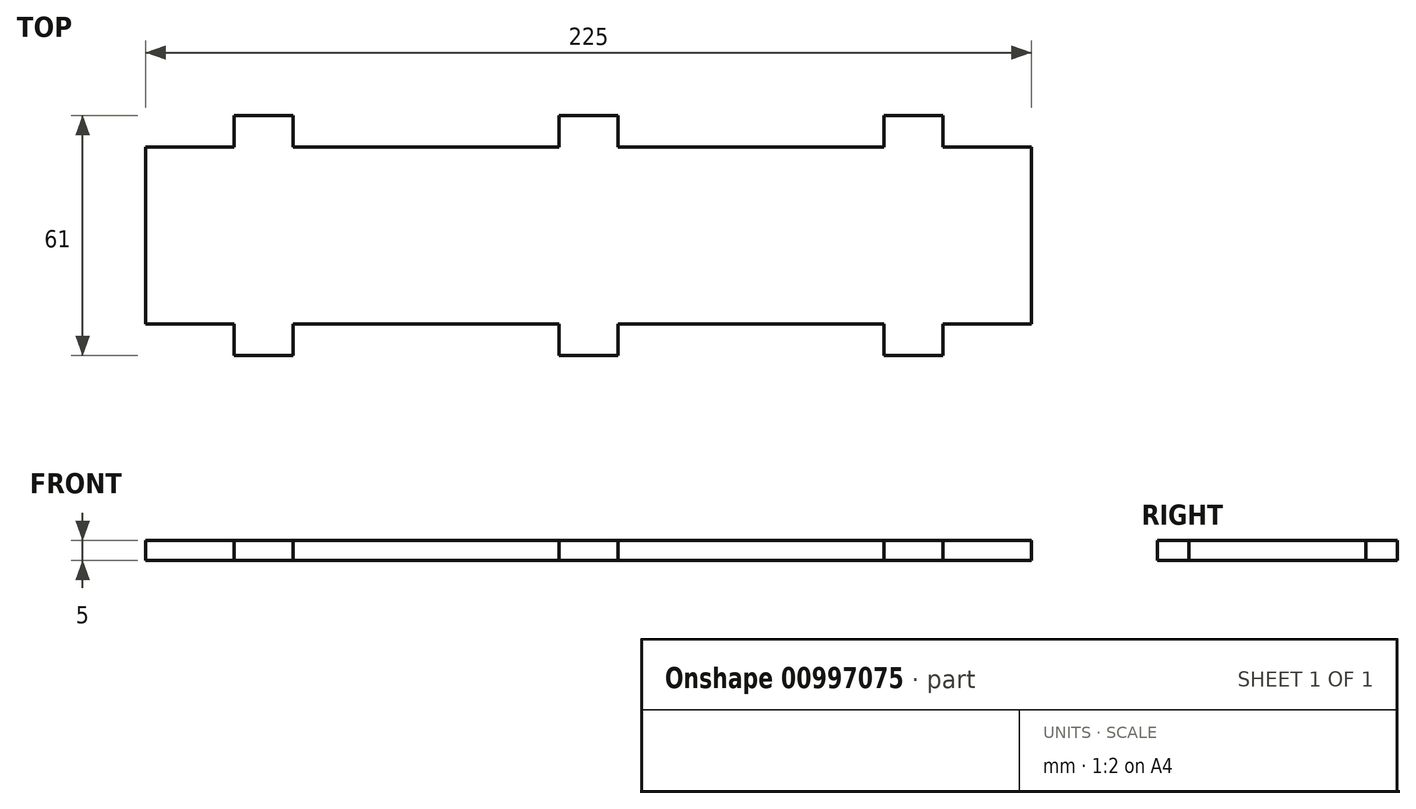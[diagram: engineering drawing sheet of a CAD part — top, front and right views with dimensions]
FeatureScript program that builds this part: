
annotation { "Feature Type Name" : "Feature", "Feature Type Description" : "" }
export const myFeature = defineFeature(function(context is Context, id is Id, definition is map)
    precondition{}
    {
        {
            var Q0;
            Q0=qCreatedBy(makeId("Top.planeOp"),FACE);
            var sketch = newSketch(context, id + "F0", { "sketchPlane" : qUnion([Q0])});
            skLineSegment(sketch, "E0", {"start": v(-112.5, 0) * mm, "end": v(-112.5, -22.5) * mm});
            skLineSegment(sketch, "E1", {"start": v(-112.5, -22.5) * mm, "end": v(-90, -22.5) * mm});
            skLineSegment(sketch, "E2", {"start": v(-90, -22.5) * mm, "end": v(-90, -30.5) * mm});
            skLineSegment(sketch, "E3", {"start": v(-90, -30.5) * mm, "end": v(-75, -30.5) * mm});
            skLineSegment(sketch, "E4", {"start": v(-75, -30.5) * mm, "end": v(-75, -22.5) * mm});
            skLineSegment(sketch, "E5", {"start": v(-75, -22.5) * mm, "end": v(-7.5, -22.5) * mm});
            skLineSegment(sketch, "E6", {"start": v(-7.5, -22.5) * mm, "end": v(-7.5, -30.5) * mm});
            skLineSegment(sketch, "E7", {"start": v(-7.5, -30.5) * mm, "end": v(7.5, -30.5) * mm});
            skLineSegment(sketch, "E8", {"start": v(7.5, -30.5) * mm, "end": v(7.5, -22.5) * mm});
            skLineSegment(sketch, "E9", {"start": v(7.5, -22.5) * mm, "end": v(75, -22.5) * mm});
            skLineSegment(sketch, "E10", {"start": v(75, -22.5) * mm, "end": v(75, -30.5) * mm});
            skLineSegment(sketch, "E11", {"start": v(75, -30.5) * mm, "end": v(90, -30.5) * mm});
            skLineSegment(sketch, "E12", {"start": v(90, -30.5) * mm, "end": v(90, -22.5) * mm});
            skLineSegment(sketch, "E13", {"start": v(90, -22.5) * mm, "end": v(112.5, -22.5) * mm});
            skLineSegment(sketch, "E14", {"start": v(112.5, -22.5) * mm, "end": v(112.5, 0) * mm});
            skLineSegment(sketch, "E15", {"start": v(112.5, 0) * mm, "end": v(-112.5, 0) * mm});
            skPoint(sketch, "E16", {"position": v(0, -30.5) * mm});
            skLineSegment(sketch, "E17.MirrorCS", {"start": v(7.5, 30.5) * mm, "end": v(7.5, 22.5) * mm});
            skLineSegment(sketch, "E18.MirrorCS", {"start": v(90, 30.5) * mm, "end": v(90, 22.5) * mm});
            skLineSegment(sketch, "E19.MirrorCS", {"start": v(-7.5, 22.5) * mm, "end": v(-7.5, 30.5) * mm});
            skLineSegment(sketch, "E20.MirrorCS", {"start": v(-75, 30.5) * mm, "end": v(-75, 22.5) * mm});
            skLineSegment(sketch, "E21.MirrorCS", {"start": v(-90, 22.5) * mm, "end": v(-90, 30.5) * mm});
            skLineSegment(sketch, "E22.MirrorCS", {"start": v(75, 22.5) * mm, "end": v(75, 30.5) * mm});
            skLineSegment(sketch, "E23.MirrorCS", {"start": v(-7.5, 30.5) * mm, "end": v(7.5, 30.5) * mm});
            skLineSegment(sketch, "E24.MirrorCS", {"start": v(7.5, 22.5) * mm, "end": v(75, 22.5) * mm});
            skLineSegment(sketch, "E25.MirrorCS", {"start": v(-112.5, 22.5) * mm, "end": v(-90, 22.5) * mm});
            skLineSegment(sketch, "E26.MirrorCS", {"start": v(-112.5, 0) * mm, "end": v(-112.5, 22.5) * mm});
            skLineSegment(sketch, "E27.MirrorCS", {"start": v(-75, 22.5) * mm, "end": v(-7.5, 22.5) * mm});
            skLineSegment(sketch, "E28.MirrorCS", {"start": v(-90, 30.5) * mm, "end": v(-75, 30.5) * mm});
            skPoint(sketch, "E29.MirrorP", {"position": v(0, 30.5) * mm});
            skLineSegment(sketch, "E30.MirrorCS", {"start": v(90, 22.5) * mm, "end": v(112.5, 22.5) * mm});
            skLineSegment(sketch, "E31.MirrorCS", {"start": v(112.5, 22.5) * mm, "end": v(112.5, 0) * mm});
            skLineSegment(sketch, "E32.MirrorCS", {"start": v(75, 30.5) * mm, "end": v(90, 30.5) * mm});
            skSolve(sketch);
        }
        {
            var Q0;
            Q0 = qSketchRegion(id + "F0", true);
            extrude(context, id + "F1", {"entities" : qUnion([Q0]), "depth" : 5 * mm, "offsetDistance" : 25 * mm});
        }
    });
